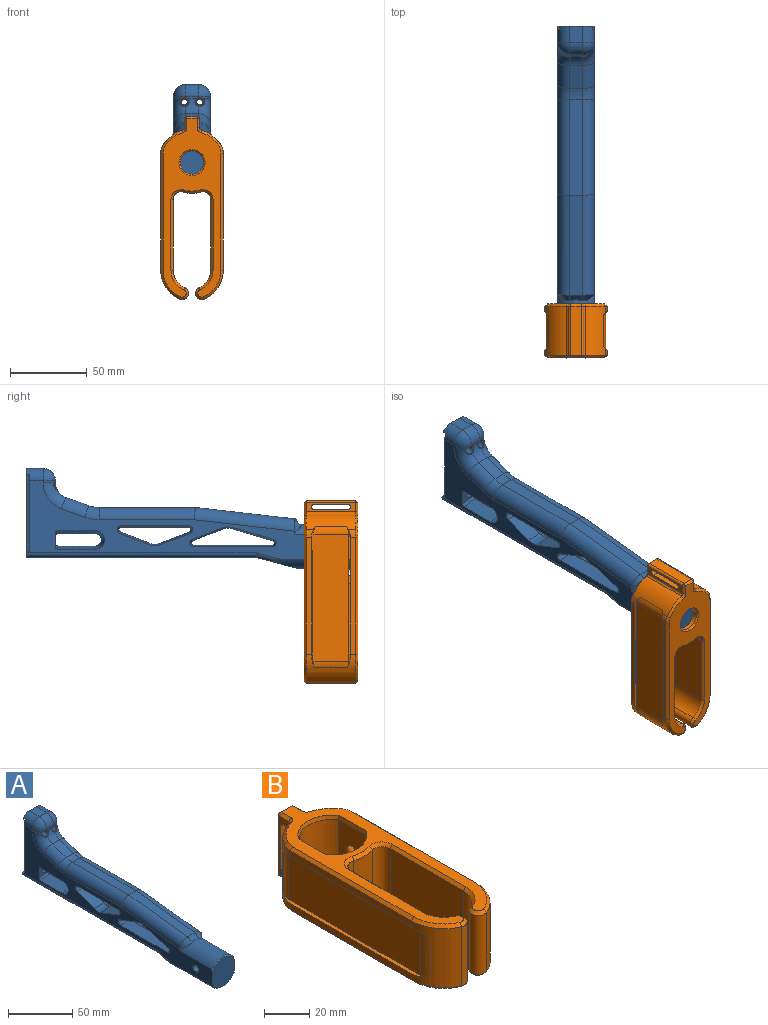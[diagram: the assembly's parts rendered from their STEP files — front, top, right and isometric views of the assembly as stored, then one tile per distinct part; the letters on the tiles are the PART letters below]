
ASSEMBLY  parts=2 mates=1
PART A: 187 faces, bbox 26.8x211x66.4 mm
  f0: plane 210.12x51.17mm, normal (-1,0,0), area 3220.6mm2, adj f2,f17,f18,f35,f46,f47,f48,f58
  f1: plane 210.12x51.17mm, normal (1,0,0), area 3220.6mm2, adj f3,f14,f15,f37,f49,f50,f51,f62
  f2: plane 8.94x7.14mm, normal (0,-1,0), area 38.2mm2, adj f0,f58,f63,f113
  f3: plane 8.94x7.14mm, normal (0,-1,0), area 38.2mm2, adj f1,f62,f67,f116
  f4: plane 7.91x5.71mm, normal (0,-1,0), area 24.2mm2, adj f58,f59,f60,f61,f62,f63,f64,f65
  f5: cylinder r=1.85mm len=9.05mm, axis (0,1,0), area 105.2mm2, adj f10,f33
  f6: cylinder r=1.85mm len=9.05mm, axis (0,1,0), area 105.2mm2, adj f10,f32
  f7: cylinder r=1.85mm len=9.05mm, axis (0,1,0), area 105.2mm2, adj f10,f30
  f8: cylinder r=1.85mm len=9.05mm, axis (0,1,0), area 105.2mm2, adj f10,f31
  f9: plane 8x1.38mm, normal (0,-1,0), area 10mm2, adj f43,f45,f78,f86,f104,f109
  f10: plane 58x23.99mm, normal (0,1,0), area 736.5mm2, adj f5,f6,f7,f8,f11,f12,f13,f20
  f11: plane 11x8mm, normal (0,0,1), area 88mm2, adj f10,f45,f80,f88
  f12: plane 149.61x18mm, normal (0,0,-1), area 2011.6mm2, adj f10,f89,f92,f93,f183,f184,f185,f186
  f13: plane 52.4x2.55mm, normal (0.94,0.34,0), area 128.8mm2, adj f10,f14,f15,f16,f36,f37
  f14: plane 50.25x4.28mm, normal (0,1,0), area 213.3mm2, adj f1,f13,f15,f16,f80
  f15: plane 4.79x1.4mm, normal (0,0,1), area 6.3mm2, adj f1,f13,f14,f37
  f16: plane 3.64x1.4mm, normal (0,0,-1), area 4.7mm2, adj f13,f14,f36,f80
  f17: plane 50.25x4.28mm, normal (0,1,0), area 213.3mm2, adj f0,f18,f19,f20,f88
  f18: plane 4.79x1.4mm, normal (0,0,1), area 6.3mm2, adj f0,f17,f20,f35
  f19: plane 3.64x1.4mm, normal (0,0,-1), area 4.7mm2, adj f17,f20,f34,f88
  f20: plane 52.4x2.55mm, normal (-0.94,0.34,0), area 128.8mm2, adj f10,f17,f18,f19,f34,f35
  f21: plane 6.7x6.7mm, normal (0,1,0), area 44.9mm2, adj f22,f23,f24,f25
  f22: plane 7x3mm, normal (1,0.05,0), area 20.6mm2, adj f10,f21,f23,f24
  f23: plane 7x3mm, normal (0,0.05,-1), area 20.6mm2, adj f10,f21,f22,f25
  f24: plane 7x3mm, normal (0,0.05,1), area 20.6mm2, adj f10,f21,f22,f25
  f25: plane 7x3mm, normal (-1,0.05,0), area 20.6mm2, adj f10,f21,f23,f24
  f26: cylinder r=2.55mm len=10.03mm, axis (0,-1,0), area 142.2mm2, adj f33,f107,f108,f109,f110
  f27: cylinder r=2.55mm len=8.75mm, axis (0,-1,0), area 140.2mm2, adj f31,f115,f116,f117,f118
  f28: cylinder r=2.55mm len=8.75mm, axis (0,-1,0), area 140.2mm2, adj f32,f111,f112,f113,f114
  f29: cylinder r=2.55mm len=10.03mm, axis (0,-1,0), area 142.2mm2, adj f30,f103,f104,f105,f106
  f30: cone r=2.55mm half-angle=45deg, axis (0,-1,0), area 13.7mm2, adj f7,f29
  f31: cone r=1.8mm half-angle=45deg, axis (0,-1,0), area 13.7mm2, adj f8,f27
  f32: cone r=2.55mm half-angle=45deg, axis (0,-1,0), area 13.7mm2, adj f6,f28
  f33: cone r=1.8mm half-angle=45deg, axis (0,-1,0), area 13.7mm2, adj f5,f26
  f34: cylinder r=1mm len=4mm, axis (1,0,0), area 5.4mm2, adj f10,f19,f20,f88
  f35: cylinder r=1mm len=5.15mm, axis (-1,0,0), area 7.9mm2, adj f0,f10,f18,f20,f89
  f36: cylinder r=1mm len=4mm, axis (-1,0,0), area 5.4mm2, adj f10,f13,f16,f80
  f37: cylinder r=1mm len=5.15mm, axis (1,0,0), area 7.9mm2, adj f1,f10,f13,f15,f92
  f38: plane 15.1x8mm, normal (0,-0.34,0.94), area 128.4mm2, adj f43,f44,f76,f84
  f39: plane 62.52x8mm, normal (0,0,1), area 500.1mm2, adj f44,f72,f74,f82
  f40: plane 24.5x3.01mm, normal (0,0,1), area 73.7mm2, adj f41,f52,f55,f60
  f41: cylinder r=4mm len=8mm, axis (-1,0,0), area 37.8mm2, adj f40,f42,f53,f56
  f42: plane 24.5x3.01mm, normal (0,0,-1), area 73.7mm2, adj f41,f54,f57,f65
  f43: cylinder r=10mm len=9.41mm, axis (-1,0,0), area 92.1mm2, adj f9,f38,f77,f85,f106,f110
  f44: cylinder r=20mm len=8mm, axis (-1,0,0), area 55.2mm2, adj f38,f39,f75,f83
  f45: cylinder r=8mm len=8mm, axis (1,0,0), area 100.5mm2, adj f9,f11,f79,f87
  f46: plane 24.5x9.51mm, normal (-0.2,0,-0.98), area 237.7mm2, adj f0,f47,f57,f63
  f47: cone r=6mm half-angle=11.3deg, axis (-1,0,0), area 153.9mm2, adj f0,f46,f48,f56
  f48: plane 24.5x9.51mm, normal (-0.2,0,0.98), area 237.7mm2, adj f0,f47,f55,f58
  f49: plane 24.5x9.51mm, normal (0.2,0,-0.98), area 237.7mm2, adj f1,f50,f54,f67
  f50: cone r=4mm half-angle=11.3deg, axis (1,0,0), area 153.9mm2, adj f1,f49,f51,f53
  f51: plane 24.5x9.51mm, normal (0.2,0,0.98), area 237.7mm2, adj f1,f50,f52,f62
  f52: cylinder r=5mm len=24.5mm, axis (0,-1,0), area 24.2mm2, adj f40,f51,f53,f61
  f53: torus R=9mm, axis (-1,0,0), area 12.5mm2, adj f41,f50,f52,f54
  f54: cylinder r=5mm len=24.5mm, axis (0,1,0), area 24.2mm2, adj f42,f49,f53,f66
  f55: cylinder r=5mm len=24.5mm, axis (0,-1,0), area 24.2mm2, adj f40,f48,f56,f59
  f56: torus R=9mm, axis (1,0,0), area 12.5mm2, adj f41,f47,f55,f57
  f57: cylinder r=5mm len=24.5mm, axis (0,1,0), area 24.2mm2, adj f42,f46,f56,f64
  f58: cylinder r=1.5mm len=9.81mm, axis (-0.98,0,-0.2), area 22.5mm2, adj f0,f2,f4,f48,f59,f114
  f59: torus R=6.5mm, axis (0,-1,0), area 2.6mm2, adj f4,f55,f58,f60
  f60: cylinder r=1.5mm len=3.01mm, axis (1,0,0), area 7.1mm2, adj f4,f40,f59,f61
  f61: torus R=6.5mm, axis (0,-1,0), area 2.6mm2, adj f4,f52,f60,f62
  f62: cylinder r=1.5mm len=9.81mm, axis (0.98,0,-0.2), area 22.5mm2, adj f1,f3,f4,f51,f61,f115
  f63: cylinder r=1.5mm len=9.81mm, axis (-0.98,0,0.2), area 22.5mm2, adj f0,f2,f4,f46,f64,f111
  f64: torus R=6.5mm, axis (0,-1,0), area 2.6mm2, adj f4,f57,f63,f65
  f65: cylinder r=1.5mm len=3.01mm, axis (-1,0,0), area 7.1mm2, adj f4,f42,f64,f66
  f66: torus R=6.5mm, axis (0,-1,0), area 2.6mm2, adj f4,f54,f65,f67
  f67: cylinder r=1.5mm len=9.81mm, axis (0.98,0,0.2), area 22.5mm2, adj f1,f3,f4,f49,f66,f118
  f68: cylinder r=14.5mm len=34.6mm, axis (0,1,0), area 894.5mm2, adj f0,f1,f96,f97,f98,f99,f100,f101
  f69: cylinder r=14.5mm len=47.39mm, axis (0,1,0), area 1091.2mm2, adj f0,f1,f71,f90,f95,f102
  f70: plane 27x24mm, normal (0,-1,0), area 547.5mm2, adj f0,f1,f101,f102
  f71: plane 27.37x18mm, normal (0,0.26,-0.97), area 440.4mm2, adj f69,f90,f93,f95
  f72: plane 65.03x8mm, normal (0,-0.11,0.99), area 523.6mm2, adj f39,f73,f81,f98
  f73: cylinder r=8mm len=66.21mm, axis (0,0.99,0.11), area 821.4mm2, adj f1,f72,f74,f99
  f74: cylinder r=8mm len=62.52mm, axis (0,1,0), area 782.7mm2, adj f1,f39,f73,f75
  f75: torus R=28mm, axis (1,0,0), area 99.3mm2, adj f1,f44,f74,f76
  f76: cylinder r=8mm len=17.81mm, axis (0,0.94,0.34), area 201.7mm2, adj f1,f38,f75,f77
  f77: torus R=18mm, axis (1,0,0), area 178.6mm2, adj f1,f43,f76,f78,f105
  f78: cylinder r=8mm len=8mm, axis (0,0,-1), area 14.9mm2, adj f1,f9,f77,f79,f103
  f79: sphere r=8mm, area 74.8mm2, adj f45,f78,f80
  f80: cylinder r=8mm len=11mm, axis (0,1,0), area 127.2mm2, adj f1,f10,f11,f14,f16,f36,f79
  f81: cylinder r=8mm len=66.21mm, axis (0,0.99,0.11), area 821.4mm2, adj f0,f72,f82,f97
  f82: cylinder r=8mm len=62.52mm, axis (0,-1,0), area 782.7mm2, adj f0,f39,f81,f83
  f83: torus R=28mm, axis (1,0,0), area 99.3mm2, adj f0,f44,f82,f84
  f84: cylinder r=8mm len=17.81mm, axis (0,-0.94,-0.34), area 201.7mm2, adj f0,f38,f83,f85
  f85: torus R=18mm, axis (1,0,0), area 178.6mm2, adj f0,f43,f84,f86,f108
  f86: cylinder r=8mm len=8mm, axis (0,0,1), area 14.9mm2, adj f0,f9,f85,f87,f107
  f87: sphere r=8mm, area 100.5mm2, adj f45,f86,f88
  f88: cylinder r=8mm len=11mm, axis (0,-1,0), area 127.2mm2, adj f0,f10,f11,f17,f19,f34,f87
  f89: cylinder r=3mm len=149.61mm, axis (0,1,0), area 705mm2, adj f0,f10,f12,f35,f91
  f90: cylinder r=3mm len=16.4mm, axis (0,0.97,0.26), area 60.4mm2, adj f0,f69,f71,f91
  f91: torus R=6mm, axis (1,0,0), area 5mm2, adj f0,f89,f90,f93
  f92: cylinder r=3mm len=149.61mm, axis (0,-1,0), area 705mm2, adj f1,f10,f12,f37,f94
  f93: cylinder r=3mm len=18mm, axis (-1,0,0), area 14.1mm2, adj f12,f71,f91,f94
  f94: torus R=6mm, axis (1,0,0), area 5mm2, adj f1,f92,f93,f95
  f95: cylinder r=3mm len=16.4mm, axis (0,0.97,0.26), area 60.4mm2, adj f1,f69,f71,f94
  f96: plane 2.03x1.67mm, normal (-0.71,-0.71,0), area 2.1mm2, adj f0,f68,f97
  f97: bspline ~8.01x7.99mm, area 48.2mm2, adj f68,f81,f96,f98
  f98: plane 9x5.13mm, normal (0,-0.75,0.67), area 40.2mm2, adj f68,f72,f97,f99
  f99: bspline ~8.01x7.99mm, area 48.2mm2, adj f68,f73,f98,f100
  f100: plane 2.03x1.67mm, normal (0.71,-0.71,0), area 2.1mm2, adj f1,f68,f99
  f101: cone r=13.5mm half-angle=45deg, axis (0,1,0), area 40.9mm2, adj f0,f1,f68,f70
  f102: cone r=13.5mm half-angle=45deg, axis (0,1,0), area 40.9mm2, adj f0,f1,f69,f70
  f103: bspline ~3.41x1.52mm, area 2.5mm2, adj f29,f78,f104,f105
  f104: cone r=3.05mm half-angle=45deg, axis (0,-1,0), area 0.9mm2, adj f9,f29,f103,f106
  f105: bspline ~4.99x4.36mm, area 5.9mm2, adj f29,f77,f103,f106
  f106: bspline ~4.76x2.25mm, area 3.7mm2, adj f29,f43,f104,f105
  f107: bspline ~3.41x1.52mm, area 2.5mm2, adj f26,f86,f108,f109
  f108: bspline ~4.99x4.36mm, area 5.9mm2, adj f26,f85,f107,f110
  f109: cone r=2.55mm half-angle=45deg, axis (0,-1,0), area 0.9mm2, adj f9,f26,f107,f110
  f110: bspline ~4.76x2.25mm, area 3.7mm2, adj f26,f43,f108,f109
  f111: bspline ~0.93x0.65mm, area 0.6mm2, adj f28,f63,f112,f113
  f112: cone r=3.05mm half-angle=45deg, axis (0,-1,0), area 4.8mm2, adj f4,f28,f111,f114
  f113: cone r=3.05mm half-angle=45deg, axis (0,-1,0), area 6.4mm2, adj f2,f28,f111,f114
  f114: bspline ~1.02x0.67mm, area 0.7mm2, adj f28,f58,f112,f113
  f115: bspline ~1.02x0.67mm, area 0.7mm2, adj f27,f62,f116,f117
  f116: cone r=2.55mm half-angle=45deg, axis (0,-1,0), area 6.4mm2, adj f3,f27,f115,f118
  f117: cone r=2.55mm half-angle=45deg, axis (0,-1,0), area 4.8mm2, adj f4,f27,f115,f118
  f118: bspline ~0.93x0.65mm, area 0.6mm2, adj f27,f67,f116,f117
  f119: cylinder r=3mm len=24mm, axis (1,0,0), area 452.4mm2, adj f0,f1
  f120: plane 43.92x3.5mm, normal (0,0,-1), area 153.8mm2, adj f128,f129,f165,f171
  f121: plane 18.9x7.31mm, normal (0,-0.36,0.93), area 70.9mm2, adj f128,f131,f162,f172
  f122: plane 18.9x7.31mm, normal (0,0.36,0.93), area 70.9mm2, adj f129,f131,f166,f168
  f123: plane 51.4x3.5mm, normal (0,0,1), area 180mm2, adj f126,f127,f156,f178
  f124: plane 26.62x7.72mm, normal (0,0.28,-0.96), area 97mm2, adj f126,f130,f160,f174
  f125: plane 19.35x7.48mm, normal (0,-0.36,-0.93), area 72.7mm2, adj f127,f130,f159,f177
  f126: cylinder r=1.5mm len=3.5mm, axis (1,0,0), area 15mm2, adj f123,f124,f158,f176
  f127: cylinder r=1.5mm len=3.5mm, axis (1,0,0), area 14.6mm2, adj f123,f125,f157,f179
  f128: cylinder r=1.5mm len=3.5mm, axis (1,0,0), area 14.6mm2, adj f120,f121,f163,f173
  f129: cylinder r=1.5mm len=3.5mm, axis (1,0,0), area 14.6mm2, adj f120,f122,f167,f169
  f130: cylinder r=10mm len=6.39mm, axis (1,0,0), area 22.8mm2, adj f124,f125,f161,f175
  f131: cylinder r=10mm len=7.21mm, axis (1,0,0), area 25.8mm2, adj f121,f122,f164,f170
  f132: plane 51.4x9.75mm, normal (-0.1,0,1), area 503.8mm2, adj f0,f133,f134,f178
  f133: cone r=2.5mm half-angle=5.7deg, axis (-1,0,0), area 54.7mm2, adj f0,f132,f135,f179
  f134: cone r=2.5mm half-angle=5.7deg, axis (-1,0,0), area 56.4mm2, adj f0,f132,f136,f176
  f135: plane 19.71x9.75mm, normal (-0.1,-0.36,-0.93), area 203.4mm2, adj f0,f133,f137,f177
  f136: plane 26.89x9.75mm, normal (-0.1,0.28,-0.96), area 271.6mm2, adj f0,f134,f137,f174
  f137: cone r=11mm half-angle=5.7deg, axis (-1,0,0), area 67.1mm2, adj f0,f135,f136,f175
  f138: plane 43.92x9.75mm, normal (-0.1,0,-1), area 430.5mm2, adj f0,f139,f140,f171
  f139: cone r=2.5mm half-angle=5.7deg, axis (-1,0,0), area 54.7mm2, adj f0,f138,f141,f169
  f140: cone r=2.5mm half-angle=5.7deg, axis (-1,0,0), area 54.7mm2, adj f0,f138,f142,f173
  f141: plane 19.25x9.75mm, normal (-0.1,0.36,0.93), area 198.6mm2, adj f0,f139,f143,f168
  f142: plane 19.25x9.75mm, normal (-0.1,-0.36,0.93), area 198.6mm2, adj f0,f140,f143,f172
  f143: cone r=11mm half-angle=5.7deg, axis (-1,0,0), area 76mm2, adj f0,f141,f142,f170
  f144: plane 19.25x9.75mm, normal (0.1,0.36,0.93), area 198.6mm2, adj f1,f145,f146,f166
  f145: cone r=2.5mm half-angle=5.7deg, axis (1,0,0), area 54.7mm2, adj f1,f144,f147,f167
  f146: cone r=11mm half-angle=5.7deg, axis (1,0,0), area 76mm2, adj f1,f144,f148,f164
  f147: plane 43.92x9.75mm, normal (0.1,0,-1), area 430.5mm2, adj f1,f145,f149,f165
  f148: plane 19.25x9.75mm, normal (0.1,-0.36,0.93), area 198.6mm2, adj f1,f146,f149,f162
  f149: cone r=2.5mm half-angle=5.7deg, axis (1,0,0), area 54.7mm2, adj f1,f147,f148,f163
  f150: plane 19.71x9.75mm, normal (0.1,-0.36,-0.93), area 203.4mm2, adj f1,f151,f152,f159
  f151: cone r=2.5mm half-angle=5.7deg, axis (1,0,0), area 54.7mm2, adj f1,f150,f153,f157
  f152: cone r=11mm half-angle=5.7deg, axis (1,0,0), area 67.1mm2, adj f1,f150,f154,f161
  f153: plane 51.4x9.75mm, normal (0.1,0,1), area 503.8mm2, adj f1,f151,f155,f156
  f154: plane 26.89x9.75mm, normal (0.1,0.28,-0.96), area 271.6mm2, adj f1,f152,f155,f160
  f155: cone r=2.5mm half-angle=5.7deg, axis (1,0,0), area 56.4mm2, adj f1,f153,f154,f158
  f156: cylinder r=5mm len=51.4mm, axis (0,-1,0), area 25.6mm2, adj f123,f153,f157,f158
  f157: torus R=6.5mm, axis (-1,0,0), area 2.1mm2, adj f127,f151,f156,f159
  f158: torus R=6.5mm, axis (-1,0,0), area 2.1mm2, adj f126,f155,f156,f160
  f159: cylinder r=5mm len=19.36mm, axis (0,0.93,-0.36), area 10.3mm2, adj f125,f150,f157,f161
  f160: cylinder r=5mm len=26.62mm, axis (0,0.96,0.28), area 13.8mm2, adj f124,f154,f158,f161
  f161: torus R=15mm, axis (-1,0,0), area 3.2mm2, adj f130,f152,f159,f160
  f162: cylinder r=5mm len=18.91mm, axis (0,-0.93,-0.36), area 10.1mm2, adj f121,f148,f163,f164
  f163: torus R=6.5mm, axis (-1,0,0), area 2.1mm2, adj f128,f149,f162,f165
  f164: torus R=15mm, axis (-1,0,0), area 3.7mm2, adj f131,f146,f162,f166
  f165: cylinder r=5mm len=43.92mm, axis (0,1,0), area 21.9mm2, adj f120,f147,f163,f167
  f166: cylinder r=5mm len=18.91mm, axis (0,-0.93,0.36), area 10.1mm2, adj f122,f144,f164,f167
  f167: torus R=6.5mm, axis (-1,0,0), area 2.1mm2, adj f129,f145,f165,f166
  f168: cylinder r=5mm len=18.91mm, axis (0,-0.93,0.36), area 10.1mm2, adj f122,f141,f169,f170
  f169: torus R=6.5mm, axis (1,0,0), area 2.1mm2, adj f129,f139,f168,f171
  f170: torus R=15mm, axis (1,0,0), area 3.7mm2, adj f131,f143,f168,f172
  f171: cylinder r=5mm len=43.92mm, axis (0,1,0), area 21.9mm2, adj f120,f138,f169,f173
  f172: cylinder r=5mm len=18.91mm, axis (0,-0.93,-0.36), area 10.1mm2, adj f121,f142,f170,f173
  f173: torus R=6.5mm, axis (1,0,0), area 2.1mm2, adj f128,f140,f171,f172
  f174: cylinder r=5mm len=26.62mm, axis (0,0.96,0.28), area 13.8mm2, adj f124,f136,f175,f176
  f175: torus R=15mm, axis (1,0,0), area 3.2mm2, adj f130,f137,f174,f177
  f176: torus R=6.5mm, axis (1,0,0), area 2.1mm2, adj f126,f134,f174,f178
  f177: cylinder r=5mm len=19.36mm, axis (0,0.93,-0.36), area 10.3mm2, adj f125,f135,f175,f179
  f178: cylinder r=5mm len=51.4mm, axis (0,-1,0), area 25.6mm2, adj f123,f132,f176,f179
  f179: torus R=6.5mm, axis (1,0,0), area 2.1mm2, adj f127,f133,f177,f178
  f180: cylinder r=2mm len=116mm, axis (0,1,0), area 571.2mm2, adj f181,f182,f184,f185
  f181: sphere r=2mm, area 8.4mm2, adj f180,f186
  f182: sphere r=2mm, area 8.4mm2, adj f180,f183
  f183: torus R=2.83mm, axis (0,0,1), area 8.8mm2, adj f12,f182,f184,f185
  f184: cylinder r=1mm len=116mm, axis (0,1,0), area 142.8mm2, adj f12,f180,f183,f186
  f185: cylinder r=1mm len=116mm, axis (0,1,0), area 142.8mm2, adj f12,f180,f183,f186
  f186: torus R=2.83mm, axis (0,0,1), area 8.8mm2, adj f12,f181,f184,f185
PART B: 108 faces, bbox 40.7x119.1x35 mm
  f0: cylinder r=10mm len=5.07mm, axis (0,0,-1), area 20mm2, adj f2,f12,f72,f80
  f1: cylinder r=10mm len=5.07mm, axis (0,0,-1), area 20mm2, adj f22,f23,f75,f99
  f2: plane 76.09x3.3mm, normal (-1,0,0), area 251.1mm2, adj f0,f3,f72,f82
  f3: cylinder r=20.34mm len=32mm, axis (0,0,-1), area 547.2mm2, adj f2,f13,f14,f56,f72,f73,f77,f84
  f4: plane 76.09x3.3mm, normal (1,0,0), area 251.1mm2, adj f21,f30,f43,f74
  f5: cylinder r=10mm len=5.07mm, axis (0,0,-1), area 20mm2, adj f12,f13,f60,f73
  f6: plane 32x5.92mm, normal (-1,0,0), area 103.1mm2, adj f31,f32,f33,f34,f35,f36,f59,f85
  f7: plane 32x5.92mm, normal (1,0,0), area 103.1mm2, adj f31,f32,f33,f34,f37,f38,f51,f93
  f8: plane 28x16.76mm, normal (1,0,0), area 444.6mm2, adj f9,f24,f26,f69,f104
  f9: cylinder r=14.8mm len=28mm, axis (0,0,-1), area 803.1mm2, adj f8,f10,f26,f105
  f10: plane 28x16.76mm, normal (-1,0,0), area 444.6mm2, adj f9,f24,f26,f67,f107
  f11: plane 32x7mm, normal (0,1,0), area 224mm2, adj f35,f38,f55,f89
  f12: cylinder r=22mm len=32mm, axis (0,0,-1), area 489.3mm2, adj f0,f5,f36,f62,f72,f73,f79,f81
  f13: plane 76.09x3.3mm, normal (-1,0,0), area 251.1mm2, adj f3,f5,f58,f73
  f14: cylinder r=4.07mm len=32mm, axis (0,0,-1), area 409.3mm2, adj f3,f15,f54,f86
  f15: cylinder r=12.2mm len=32mm, axis (0,0,-1), area 455.4mm2, adj f14,f16,f52,f88
  f16: plane 46.06x32mm, normal (1,0,0), area 1473.9mm2, adj f15,f28,f50,f90
  f17: cylinder r=20mm len=32mm, axis (0,0,-1), area 373.9mm2, adj f28,f29,f46,f94
  f18: plane 46.06x32mm, normal (-1,0,0), area 1473.9mm2, adj f19,f29,f42,f98
  f19: cylinder r=12.2mm len=32mm, axis (0,0,-1), area 455.4mm2, adj f18,f20,f40,f100
  f20: cylinder r=4.07mm len=32mm, axis (0,0,-1), area 409.3mm2, adj f19,f21,f39,f102
  f21: cylinder r=20.34mm len=32mm, axis (0,0,-1), area 547.2mm2, adj f4,f20,f22,f41,f74,f75,f76,f103
  f22: plane 76.09x3.3mm, normal (1,0,0), area 251.1mm2, adj f1,f21,f75,f101
  f23: cylinder r=22mm len=32mm, axis (0,0,-1), area 489.3mm2, adj f1,f30,f37,f47,f74,f75,f78,f97
  f24: cylinder r=14.8mm len=28mm, axis (0,0,-1), area 803.1mm2, adj f8,f10,f26,f106
  f25: plane 116.06x37.68mm, normal (0,0,1), area 1466.6mm2, adj f80,f81,f82,f83,f84,f85,f86,f88
  f26: plane 29.6x24.4mm, normal (0,0,1), area 402mm2, adj f8,f9,f10,f24,f65
  f27: plane 116.06x37.68mm, normal (0,0,-1), area 1914.8mm2, adj f39,f40,f41,f42,f43,f44,f45,f46
  f28: cylinder r=5mm len=32mm, axis (0,0,-1), area 298.1mm2, adj f16,f17,f48,f92
  f29: cylinder r=5mm len=32mm, axis (0,0,-1), area 298.1mm2, adj f17,f18,f44,f96
  f30: cylinder r=10mm len=5.07mm, axis (0,0,-1), area 20mm2, adj f4,f23,f45,f74
  f31: plane 21.9x10mm, normal (0,1,0), area 219mm2, adj f6,f7,f33,f34
  f32: plane 21.9x10mm, normal (0,-1,0), area 219mm2, adj f6,f7,f33,f34
  f33: cylinder r=1.75mm len=10mm, axis (1,0,0), area 55mm2, adj f6,f7,f31,f32
  f34: cylinder r=1.75mm len=10mm, axis (-1,0,0), area 55mm2, adj f6,f7,f31,f32
  f35: cylinder r=1.5mm len=32mm, axis (0,0,-1), area 75.4mm2, adj f6,f11,f57,f87
  f36: cylinder r=1.5mm len=32mm, axis (0,0,-1), area 61.9mm2, adj f6,f12,f61,f83
  f37: cylinder r=1.5mm len=32mm, axis (0,0,-1), area 61.9mm2, adj f7,f23,f49,f95
  f38: cylinder r=1.5mm len=32mm, axis (0,0,1), area 75.4mm2, adj f7,f11,f53,f91
  f39: cone r=4.07mm half-angle=45deg, axis (0,0,1), area 22.1mm2, adj f20,f27,f40,f41
  f40: cone r=12.2mm half-angle=45deg, axis (0,0,-1), area 32.1mm2, adj f19,f27,f39,f42
  f41: cone r=18.84mm half-angle=45deg, axis (0,0,1), area 48.8mm2, adj f21,f27,f39,f43
  f42: plane 46.06x1.5mm, normal (-0.71,0,-0.71), area 97.7mm2, adj f18,f27,f40,f44
  f43: plane 76.09x1.5mm, normal (0.71,0,-0.71), area 161.4mm2, adj f4,f27,f41,f45
  f44: cone r=6.5mm half-angle=45deg, axis (0,0,-1), area 22.7mm2, adj f27,f29,f42,f46
  f45: cone r=8.5mm half-angle=45deg, axis (0,0,1), area 10.4mm2, adj f27,f30,f43,f47
  f46: cone r=20mm half-angle=45deg, axis (0,0,1), area 23.9mm2, adj f17,f27,f44,f48
  f47: cone r=20.5mm half-angle=45deg, axis (0,0,1), area 34.2mm2, adj f23,f27,f45,f49
  f48: cone r=6.5mm half-angle=45deg, axis (0,0,-1), area 22.7mm2, adj f27,f28,f46,f50
  f49: cone r=3mm half-angle=45deg, axis (0,0,-1), area 6.2mm2, adj f27,f37,f47,f51
  f50: plane 46.06x1.5mm, normal (0.71,0,-0.71), area 97.7mm2, adj f16,f27,f48,f52
  f51: plane 5.92x1.5mm, normal (0.71,0,-0.71), area 12.6mm2, adj f7,f27,f49,f53
  f52: cone r=13.7mm half-angle=45deg, axis (0,0,-1), area 32.1mm2, adj f15,f27,f50,f54
  f53: cone r=1.5mm half-angle=45deg, axis (0,0,1), area 2.5mm2, adj f38,f51,f55
  f54: cone r=2.57mm half-angle=45deg, axis (0,0,1), area 22.1mm2, adj f14,f27,f52,f56
  f55: plane 7x1.5mm, normal (0,0.71,-0.71), area 14.8mm2, adj f11,f27,f53,f57
  f56: cone r=20.34mm half-angle=45deg, axis (0,0,1), area 48.8mm2, adj f3,f27,f54,f58
  f57: cone r=1.5mm half-angle=45deg, axis (0,0,1), area 2.5mm2, adj f35,f55,f59
  f58: plane 76.09x1.5mm, normal (-0.71,0,-0.71), area 161.4mm2, adj f13,f27,f56,f60
  f59: plane 5.92x1.5mm, normal (-0.71,0,-0.71), area 12.6mm2, adj f6,f27,f57,f61
  f60: cone r=8.5mm half-angle=45deg, axis (0,0,1), area 10.4mm2, adj f5,f27,f58,f62
  f61: cone r=3mm half-angle=45deg, axis (0,0,-1), area 6.2mm2, adj f27,f36,f59,f62
  f62: cone r=20.5mm half-angle=45deg, axis (0,0,1), area 34.2mm2, adj f12,f27,f60,f61
  f63: cylinder r=7.5mm len=15mm, axis (0,0,-1), area 141.4mm2, adj f64,f65
  f64: cone r=7.5mm half-angle=45deg, axis (0,0,-1), area 71.1mm2, adj f27,f63
  f65: cone r=8.5mm half-angle=45deg, axis (0,0,1), area 71.1mm2, adj f26,f63
  f66: plane 1x1mm, normal (-1,0,0), area 0.8mm2, adj f67
  f67: torus R=0.5mm, axis (-1,0,0), area 44.6mm2, adj f10,f66
  f68: plane 1x1mm, normal (1,0,0), area 0.8mm2, adj f69
  f69: torus R=0.5mm, axis (1,0,0), area 44.6mm2, adj f8,f68
  f70: plane 82.64x23.4mm, normal (1,0,0), area 1933.9mm2, adj f74,f75,f76,f78
  f71: plane 82.64x23.4mm, normal (-1,0,0), area 1933.9mm2, adj f72,f73,f77,f79
  f72: plane 91.62x2.52mm, normal (-0.71,0,-0.71), area 118.8mm2, adj f0,f2,f3,f12,f71,f77,f79
  f73: plane 91.62x2.52mm, normal (-0.71,0,0.71), area 118.8mm2, adj f3,f5,f12,f13,f71,f77,f79
  f74: plane 91.62x2.52mm, normal (0.71,0,0.71), area 118.8mm2, adj f4,f21,f23,f30,f70,f76,f78
  f75: plane 91.62x2.52mm, normal (0.71,0,-0.71), area 118.8mm2, adj f1,f21,f22,f23,f70,f76,f78
  f76: cylinder r=10mm len=23.4mm, axis (0,0,-1), area 100.9mm2, adj f21,f70,f74,f75
  f77: cylinder r=10mm len=23.4mm, axis (0,0,-1), area 100.9mm2, adj f3,f71,f72,f73
  f78: cylinder r=8mm len=23.4mm, axis (0,0,-1), area 112.1mm2, adj f23,f70,f74,f75
  f79: cylinder r=8mm len=23.4mm, axis (0,0,-1), area 112.1mm2, adj f12,f71,f72,f73
  f80: cone r=8.5mm half-angle=45deg, axis (0,0,-1), area 10.4mm2, adj f0,f25,f81,f82
  f81: cone r=22mm half-angle=45deg, axis (0,0,-1), area 34.2mm2, adj f12,f25,f80,f83
  f82: plane 76.09x1.5mm, normal (-0.71,0,0.71), area 161.4mm2, adj f2,f25,f80,f84
  f83: cone r=3mm half-angle=45deg, axis (0,0,1), area 6.2mm2, adj f25,f36,f81,f85
  f84: cone r=18.84mm half-angle=45deg, axis (0,0,-1), area 48.8mm2, adj f3,f25,f82,f86
  f85: plane 5.92x1.5mm, normal (-0.71,0,0.71), area 12.6mm2, adj f6,f25,f83,f87
  f86: cone r=4.07mm half-angle=45deg, axis (0,0,-1), area 22.1mm2, adj f14,f25,f84,f88
  f87: cone r=1.5mm half-angle=45deg, axis (0,0,-1), area 2.5mm2, adj f35,f85,f89
  f88: cone r=12.2mm half-angle=45deg, axis (0,0,1), area 32.1mm2, adj f15,f25,f86,f90
  f89: plane 7x1.5mm, normal (0,0.71,0.71), area 14.8mm2, adj f11,f25,f87,f91
  f90: plane 46.06x1.5mm, normal (0.71,0,0.71), area 97.7mm2, adj f16,f25,f88,f92
  f91: cone r=1.5mm half-angle=45deg, axis (0,0,-1), area 2.5mm2, adj f38,f89,f93
  f92: cone r=6.5mm half-angle=45deg, axis (0,0,1), area 22.7mm2, adj f25,f28,f90,f94
  f93: plane 5.92x1.5mm, normal (0.71,0,0.71), area 12.6mm2, adj f7,f25,f91,f95
  f94: cone r=18.5mm half-angle=45deg, axis (0,0,-1), area 23.9mm2, adj f17,f25,f92,f96
  f95: cone r=3mm half-angle=45deg, axis (0,0,1), area 6.2mm2, adj f25,f37,f93,f97
  f96: cone r=6.5mm half-angle=45deg, axis (0,0,1), area 22.7mm2, adj f25,f29,f94,f98
  f97: cone r=22mm half-angle=45deg, axis (0,0,-1), area 34.2mm2, adj f23,f25,f95,f99
  f98: plane 46.06x1.5mm, normal (-0.71,0,0.71), area 97.7mm2, adj f18,f25,f96,f100
  f99: cone r=8.5mm half-angle=45deg, axis (0,0,-1), area 10.4mm2, adj f1,f25,f97,f101
  f100: cone r=13.7mm half-angle=45deg, axis (0,0,1), area 32.1mm2, adj f19,f25,f98,f102
  f101: plane 76.09x1.5mm, normal (0.71,0,0.71), area 161.4mm2, adj f22,f25,f99,f103
  f102: cone r=2.57mm half-angle=45deg, axis (0,0,-1), area 22.1mm2, adj f20,f25,f100,f103
  f103: cone r=20.34mm half-angle=45deg, axis (0,0,-1), area 48.8mm2, adj f21,f25,f101,f102
  f104: plane 17.07x2mm, normal (0.97,0,0.24), area 34.9mm2, adj f8,f25,f105,f106
  f105: cone r=14.8mm half-angle=14deg, axis (0,0,1), area 60.4mm2, adj f9,f25,f104,f107
  f106: cone r=14.8mm half-angle=14deg, axis (0,0,1), area 60.4mm2, adj f24,f25,f104,f107
  f107: plane 17.07x2mm, normal (-0.97,0,0.24), area 34.9mm2, adj f10,f25,f105,f106
PLACE A t=(-1.32,70.18,7.74)mm
PLACE B rot(axis=(0,-0.71,-0.71),180deg) t=(-1.32,-140.64,-14.16)mm
MATE cylindrical B.f63 <-> A.f69  axis (0,1,0) through (-1.32,-144.64,-14.16)mm
